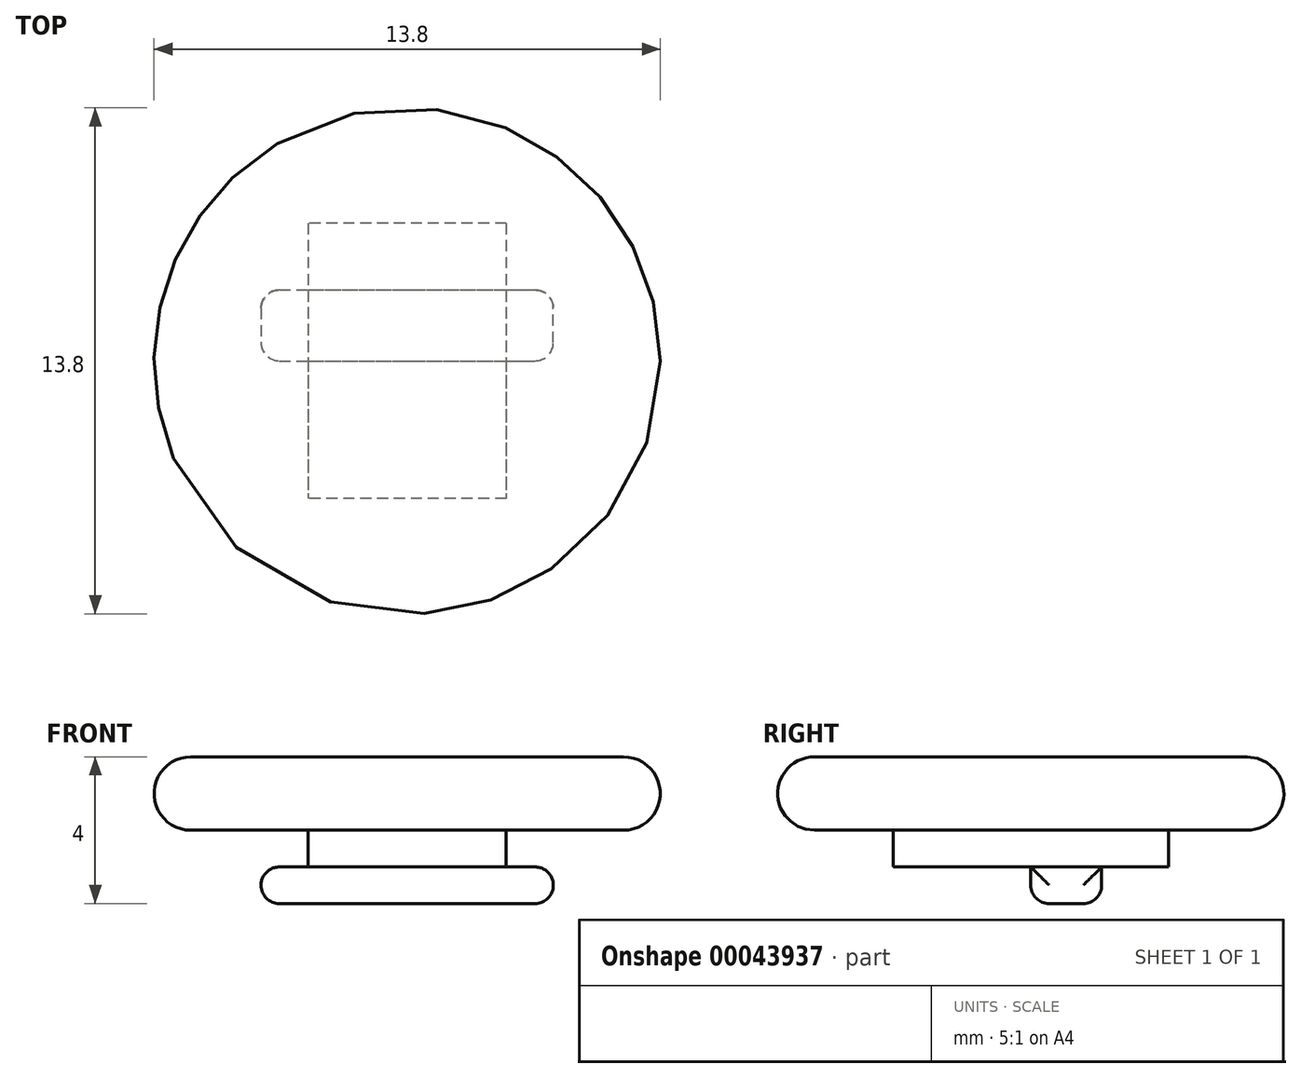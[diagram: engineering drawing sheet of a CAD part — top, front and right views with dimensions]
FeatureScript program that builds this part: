
annotation { "Feature Type Name" : "Feature", "Feature Type Description" : "" }
export const myFeature = defineFeature(function(context is Context, id is Id, definition is map)
    precondition{}
    {
        {
            var Q0;
            Q0=qCreatedBy(makeId("Top.planeOp"),FACE);
            var sketch = newSketch(context, id + "F0", { "sketchPlane" : qUnion([Q0])});
            skCircle(sketch, "E0", {"center": v(0, 0) * mm, "radius": 6.9 * mm});
            skSolve(sketch);
        }
        {
            var Q0;
            Q0 = qSketchRegion(id + "F0", true);
            extrude(context, id + "F1", {"entities" : qUnion([Q0]), "depth" : 2 * mm});
        }
        {
            var Q0;
            Q0=makeQuery(id+"F1.opExtrude","SWEPT_FACE",FACE,{"disambiguationData":[OSD([sQuery(id+"F0.wireOp",EDGE,"E0")])]});
            var Q1;
            Q1=makeQuery(id+"F1.opExtrude","CAP_EDGE",EDGE,{"disambiguationData":[OSD([sQuery(id+"F0.wireOp",EDGE,"E0")])],"isStart":false});
            var Q2;
            Q2=makeQuery(id+"F1.opExtrude","CAP_EDGE",EDGE,{"disambiguationData":[OSD([sQuery(id+"F0.wireOp",EDGE,"E0")])],"isStart":true});
            fillet(context, id + "F2", {"entities" : qUnion([Q0, Q1, Q2]), "radius" : 1 * mm, "tangentPropagation" : true, "allowEdgeOverflow" : false});
        }
        {
            var Q0;
            Q0=makeQuery(id+"F0.imprint","IMPRINT",FACE,{"disambiguationData":[TD([[makeQuery(id+"F0.imprint","IMPRINT",EDGE,{"derivedFrom":sQuery(id+"F0.wireOp",EDGE,"E0")}),1.0]])]});
            var sketch = newSketch(context, id + "F3", { "sketchPlane" : qUnion([Q0])});
            skLineSegment(sketch, "E1.rect.bottom", {"start": v(2.7, 3.75) * mm, "end": v(-2.7, 3.75) * mm});
            skLineSegment(sketch, "E1.rect.top", {"start": v(2.7, -3.75) * mm, "end": v(-2.7, -3.75) * mm});
            skLineSegment(sketch, "E1.rect.left", {"start": v(2.7, 3.75) * mm, "end": v(2.7, -3.75) * mm});
            skLineSegment(sketch, "E1.rect.right", {"start": v(-2.7, 3.75) * mm, "end": v(-2.7, -3.75) * mm});
            skPoint(sketch, "E1.rect.middle", {"position": v(0, 0) * mm});
            skSolve(sketch);
        }
        {
            var Q0;
            Q0 = qSketchRegion(id + "F3", true);
            extrude(context, id + "F4", {"entities" : qUnion([Q0]), "operationType" : NewBodyOperationType.ADD, "oppositeDirection" : true, "depth" : 1 * mm});
        }
        {
            var Q0;
            Q0=makeQuery(id+"F4.opExtrude","CAP_FACE",FACE,{"disambiguationData":[OSD([sQuery(id+"F3.wireOp",EDGE,"E1.rect.bottom"),sQuery(id+"F3.wireOp",EDGE,"E1.rect.top"),sQuery(id+"F3.wireOp",EDGE,"E1.rect.left"),sQuery(id+"F3.wireOp",EDGE,"E1.rect.right")])],"isStart":false});
            var sketch = newSketch(context, id + "F5", { "sketchPlane" : qUnion([Q0])});
            skLineSegment(sketch, "E2.bottom", {"start": v(-3.98, 0) * mm, "end": v(3.98, 0) * mm});
            skLineSegment(sketch, "E2.top", {"start": v(-3.98, -1.93) * mm, "end": v(3.98, -1.93) * mm});
            skLineSegment(sketch, "E2.left", {"start": v(-3.98, 0) * mm, "end": v(-3.98, -1.93) * mm});
            skLineSegment(sketch, "E2.right", {"start": v(3.98, 0) * mm, "end": v(3.98, -1.93) * mm});
            skSolve(sketch);
        }
        {
            var Q0;
            Q0 = qSketchRegion(id + "F5", true);
            extrude(context, id + "F6", {"entities" : qUnion([Q0]), "operationType" : NewBodyOperationType.ADD, "depth" : 1 * mm});
        }
        {
            var Q0;
            Q0=makeQuery(id+"F6.opExtrude","CAP_EDGE",EDGE,{"disambiguationData":[OSD([sQuery(id+"F5.wireOp",EDGE,"E2.bottom")])],"isStart":false});
            var Q1;
            Q1=makeQuery(id+"F6.opExtrude","CAP_EDGE",EDGE,{"disambiguationData":[OSD([sQuery(id+"F5.wireOp",EDGE,"E2.top")])],"isStart":false});
            fillet(context, id + "F7", {"entities" : qUnion([Q0, Q1]), "radius" : .5 * mm, "tangentPropagation" : true, "allowEdgeOverflow" : false});
        }
        {
            var Q0;
            Q0=makeQuery(id+"F6.opExtrude","CAP_EDGE",EDGE,{"disambiguationData":[OSD([sQuery(id+"F5.wireOp",EDGE,"E2.left")])],"isStart":true});
            var Q1;
            Q1=makeQuery(id+"F6.opExtrude","CAP_EDGE",EDGE,{"disambiguationData":[OSD([sQuery(id+"F5.wireOp",EDGE,"E2.left")])],"isStart":false});
            fillet(context, id + "F8", {"entities" : qUnion([Q0, Q1]), "radius" : .5 * mm, "tangentPropagation" : true, "allowEdgeOverflow" : false});
        }
        {
            var Q0;
            Q0=makeQuery(id+"F6.opExtrude","CAP_EDGE",EDGE,{"disambiguationData":[OSD([sQuery(id+"F5.wireOp",EDGE,"E2.right")])],"isStart":false});
            var Q1;
            Q1=makeQuery(id+"F6.opExtrude","CAP_EDGE",EDGE,{"disambiguationData":[OSD([sQuery(id+"F5.wireOp",EDGE,"E2.right")])],"isStart":true});
            fillet(context, id + "F9", {"entities" : qUnion([Q0, Q1]), "radius" : .5 * mm, "tangentPropagation" : true, "allowEdgeOverflow" : false});
        }
    });
